FREECAD ASSEMBLY — COMPONENT RECIPES ("splitflap")

This assembly document has 10 components, labeled P0..P9 below (a component is one placed body or linked part). 0 of them carry a construction recipe — the FreeCAD feature program that regenerates the part from scratch, quoted from this document or its linked companion documents; the rest are supplied as boundary geometry only. No exploded tour is included for this assembly.
COMPONENT P0 — geometry summary ("Front"; no construction recipe available for this part):
  bounding box: 160.0 x 80.0 x 13.0 mm
  tessellated surface: 1,368 triangles
  volume: 31480 mm^3 (19% of its bounding box)
  symmetry: mirror-symmetric across its x mid-plane
COMPONENT P1 — geometry summary ("LeftSide"; no construction recipe available for this part):
  bounding box: 160.0 x 105.0 x 4.0 mm
  tessellated surface: 7,308 triangles
  volume: 31949 mm^3 (48% of its bounding box)
  symmetry: mirror-symmetric across its x mid-plane
COMPONENT P2 — geometry summary ("RightSide"; no construction recipe available for this part):
  bounding box: 160.0 x 105.0 x 4.0 mm
  tessellated surface: 17,262 triangles
  volume: 44803 mm^3 (67% of its bounding box)
COMPONENT P3 — geometry summary ("BodySpacerBottom"; no construction recipe available for this part):
  bounding box: 72.0 x 10.0 x 10.0 mm
  tessellated surface: 1,008 triangles
  volume: 5146 mm^3 (71% of its bounding box)
  symmetry: revolution-symmetric about the x axis through its bounding-box center; mirror-symmetric across its x mid-plane, y mid-plane
COMPONENT P4 — geometry summary ("BodySpacerTop"; no construction recipe available for this part):
  bounding box: 72.0 x 10.0 x 10.0 mm
  tessellated surface: 1,008 triangles
  volume: 5146 mm^3 (71% of its bounding box)
  symmetry: revolution-symmetric about the x axis through its bounding-box center; mirror-symmetric across its x mid-plane, y mid-plane
COMPONENT P5 — geometry summary ("MotorSpacer"; no construction recipe available for this part):
  bounding box: 12.0 x 9.2 x 9.2 mm
  tessellated surface: 1,008 triangles
  volume: 701 mm^3 (69% of its bounding box)
  symmetry: revolution-symmetric about the x axis through its bounding-box center; 2-fold rotationally symmetric about the y axis; 2-fold rotationally symmetric about the z axis; mirror-symmetric across its x mid-plane, y mid-plane
COMPONENT P6 — geometry summary ("MotorSpacer001"; no construction recipe available for this part):
  bounding box: 12.0 x 9.2 x 9.2 mm
  tessellated surface: 1,008 triangles
  volume: 701 mm^3 (69% of its bounding box)
  symmetry: revolution-symmetric about the x axis through its bounding-box center; 2-fold rotationally symmetric about the y axis; 2-fold rotationally symmetric about the z axis; mirror-symmetric across its x mid-plane, y mid-plane
COMPONENT P7 — geometry summary ("MotorSpacer002"; no construction recipe available for this part):
  bounding box: 12.0 x 9.2 x 9.2 mm
  tessellated surface: 1,008 triangles
  volume: 701 mm^3 (69% of its bounding box)
  symmetry: revolution-symmetric about the x axis through its bounding-box center; 2-fold rotationally symmetric about the y axis; 2-fold rotationally symmetric about the z axis; mirror-symmetric across its x mid-plane, y mid-plane
COMPONENT P8 — geometry summary ("MotorSpacer003"; no construction recipe available for this part):
  bounding box: 12.0 x 9.2 x 9.2 mm
  tessellated surface: 1,008 triangles
  volume: 701 mm^3 (69% of its bounding box)
  symmetry: revolution-symmetric about the x axis through its bounding-box center; 2-fold rotationally symmetric about the y axis; 2-fold rotationally symmetric about the z axis; mirror-symmetric across its x mid-plane, y mid-plane
COMPONENT P9 — geometry summary ("17HS13-0404D"; no construction recipe available for this part):
  bounding box: 63.0 x 60.3 x 42.3 mm
  tessellated surface: 85,216 triangles
  volume: 57704 mm^3 (36% of its bounding box)
  symmetry: mirror-symmetric across its y mid-plane
PROVENANCE & LICENSES
A FreeCAD (.FCStd) document from a public repository crawl; recipes are the document's own serialized feature recipes (and, for linked parts, companion documents' recipes).
License: mit.
